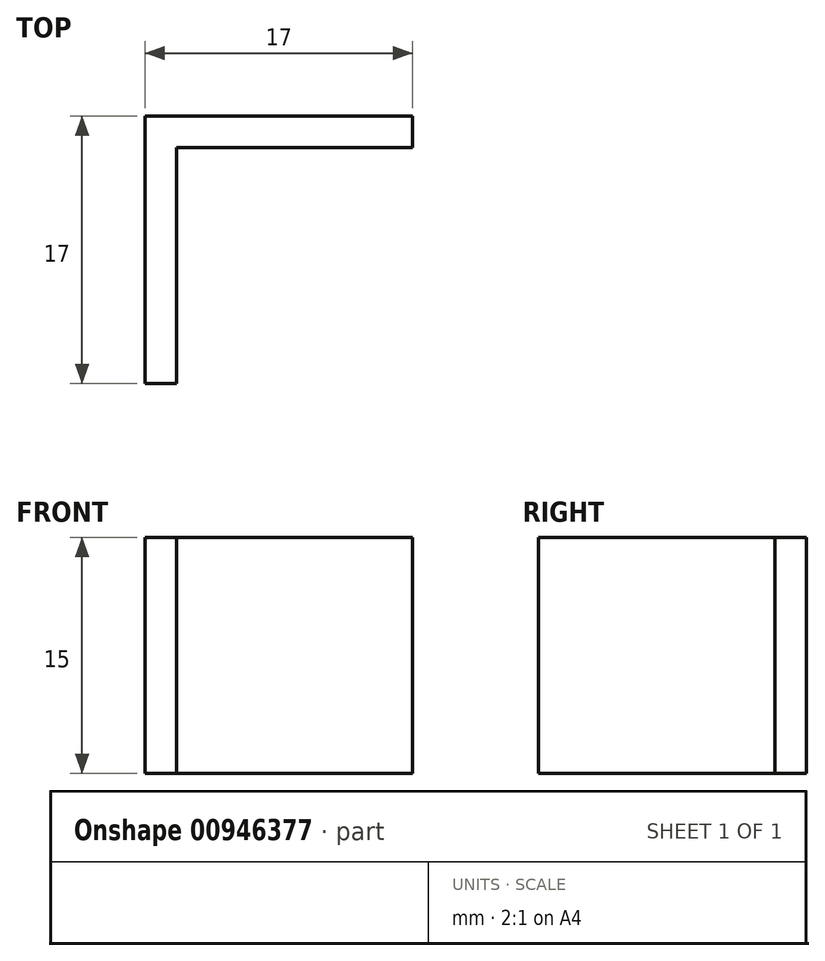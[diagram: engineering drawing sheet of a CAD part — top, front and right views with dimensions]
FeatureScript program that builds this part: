
annotation { "Feature Type Name" : "Feature", "Feature Type Description" : "" }
export const myFeature = defineFeature(function(context is Context, id is Id, definition is map)
    precondition{}
    {
        {
            var Q0;
            Q0=qCreatedBy(makeId("Top.planeOp"),FACE);
            var sketch = newSketch(context, id + "F0", { "sketchPlane" : qUnion([Q0])});
            skLineSegment(sketch, "E0", {"start": v(0, 0) * mm, "end": v(0, -17) * mm});
            skLineSegment(sketch, "E1", {"start": v(0, -17) * mm, "end": v(2, -17) * mm});
            skLineSegment(sketch, "E2", {"start": v(2, -17) * mm, "end": v(2, -2) * mm});
            skLineSegment(sketch, "E3", {"start": v(2, -2) * mm, "end": v(17, -2) * mm});
            skLineSegment(sketch, "E4", {"start": v(17, -2) * mm, "end": v(17, 0) * mm});
            skLineSegment(sketch, "E5", {"start": v(17, 0) * mm, "end": v(0, 0) * mm});
            skSolve(sketch);
        }
        {
            var Q0;
            Q0 = qSketchRegion(id + "F0", true);
            extrude(context, id + "F1", {"entities" : qUnion([Q0]), "depth" : 15 * mm, "offsetDistance" : 25 * mm});
        }
    });
